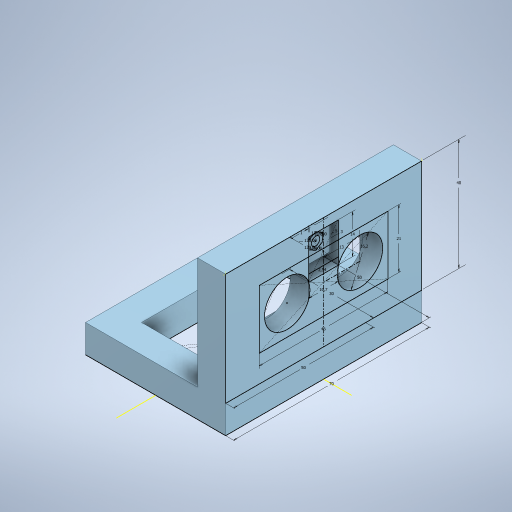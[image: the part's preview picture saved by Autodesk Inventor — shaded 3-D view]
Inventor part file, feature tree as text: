
AUTODESK INVENTOR PART (.ipt)
format: ipt  version: 2024.2 (Build 282272000, 272)  size: 339,456 bytes
history: native  units: mm
features: extrude x5, sketch x2
ambient origin geometry x8: Origin, YZ Plane, XZ Plane, XY Plane, X Axis, Y Axis, Z Axis, Center Point
bodies: Body1 (feature_tree)
feature tree (7):
  sketch  "Szkic7"
  extrude  "Wyciągnięcie proste6"  Depth=30.0mm
  extrude  "Wyciągnięcie proste7"  Depth=50.0mm
  sketch  "Szkic8"
  extrude  "Wyciągnięcie proste8"  Depth=50.0mm
  extrude  "Wyciągnięcie proste9"  Depth=70.0mm
  extrude  "Wyciągnięcie proste10"  Depth=10.0mm TaperAngle=0.0deg
